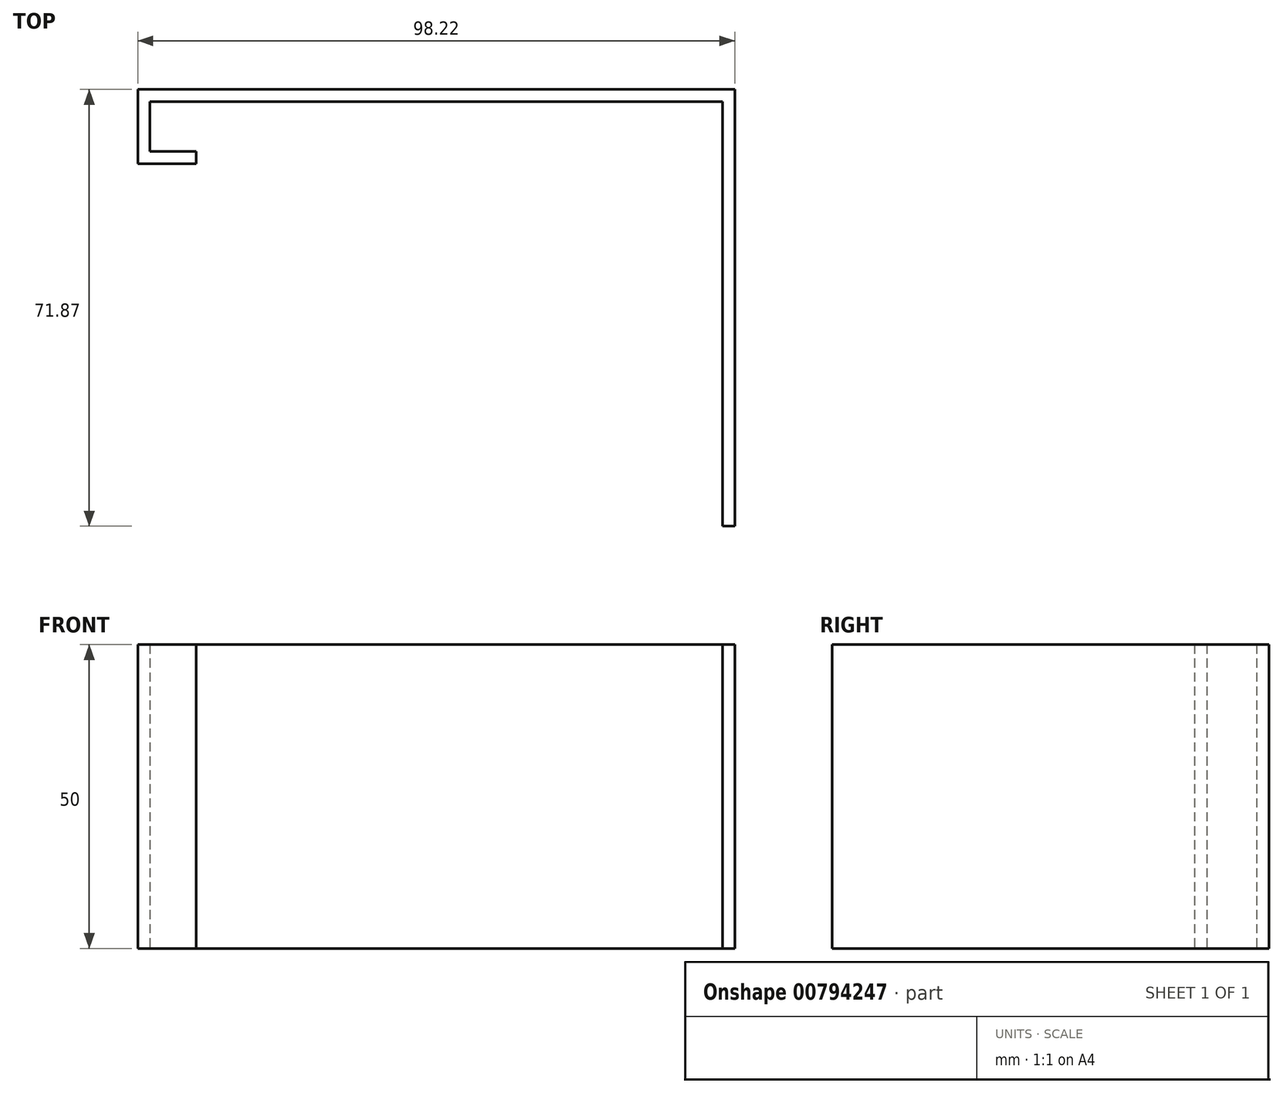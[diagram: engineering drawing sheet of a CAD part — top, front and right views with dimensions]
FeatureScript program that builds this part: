
annotation { "Feature Type Name" : "Feature", "Feature Type Description" : "" }
export const myFeature = defineFeature(function(context is Context, id is Id, definition is map)
    precondition{}
    {
        {
            var Q0;
            Q0=qCreatedBy(makeId("Top.planeOp"),FACE);
            var sketch = newSketch(context, id + "F0", { "sketchPlane" : qUnion([Q0])});
            skLineSegment(sketch, "E0.bottom", {"start": v(0, 0) * mm, "end": v(-2, 0) * mm});
            skLineSegment(sketch, "E0.top", {"start": v(0, -71.87) * mm, "end": v(-2, -71.87) * mm});
            skLineSegment(sketch, "E0.left", {"start": v(0, 0) * mm, "end": v(0, -71.87) * mm});
            skLineSegment(sketch, "E0.right", {"start": v(-2, 0) * mm, "end": v(-2, -71.87) * mm});
            skLineSegment(sketch, "E1.bottom", {"start": v(0, 0) * mm, "end": v(-98.22, 0) * mm});
            skLineSegment(sketch, "E1.top", {"start": v(0, -2) * mm, "end": v(-98.22, -2) * mm});
            skLineSegment(sketch, "E1.left", {"start": v(0, 0) * mm, "end": v(0, -2) * mm});
            skLineSegment(sketch, "E1.right", {"start": v(-98.22, 0) * mm, "end": v(-98.22, -2) * mm});
            skLineSegment(sketch, "E2.bottom", {"start": v(-98.22, 0) * mm, "end": v(-96.22, 0) * mm});
            skLineSegment(sketch, "E2.top", {"start": v(-98.22, -12.2) * mm, "end": v(-96.22, -12.2) * mm});
            skLineSegment(sketch, "E2.left", {"start": v(-98.22, 0) * mm, "end": v(-98.22, -12.2) * mm});
            skLineSegment(sketch, "E2.right", {"start": v(-96.22, 0) * mm, "end": v(-96.22, -12.2) * mm});
            skLineSegment(sketch, "E3.bottom", {"start": v(-98.22, -12.2) * mm, "end": v(-88.61, -12.2) * mm});
            skLineSegment(sketch, "E3.top", {"start": v(-98.22, -10.2) * mm, "end": v(-88.61, -10.2) * mm});
            skLineSegment(sketch, "E3.left", {"start": v(-98.22, -12.2) * mm, "end": v(-98.22, -10.2) * mm});
            skLineSegment(sketch, "E3.right", {"start": v(-88.61, -12.2) * mm, "end": v(-88.61, -10.2) * mm});
            skSolve(sketch);
        }
        {
            var Q0;
            Q0 = qSketchRegion(id + "F0", true);
            extrude(context, id + "F1", {"entities" : qUnion([Q0]), "depth" : 50 * mm, "offsetDistance" : 25 * mm});
        }
    });
